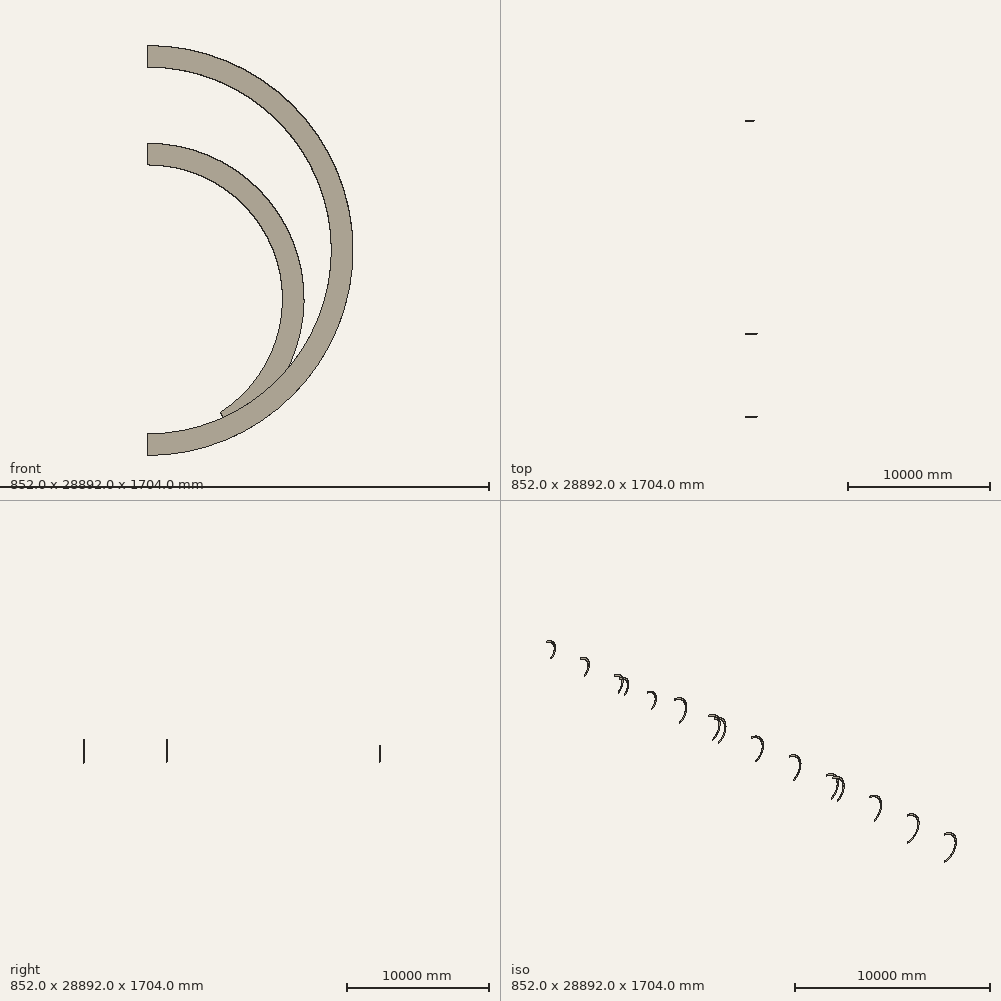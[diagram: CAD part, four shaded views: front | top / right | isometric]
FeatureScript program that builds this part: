
annotation { "Feature Type Name" : "Feature", "Feature Type Description" : "" }
export const myFeature = defineFeature(function(context is Context, id is Id, definition is map)
    precondition{}
    {
        {
            var Q0;
            Q0=qCreatedBy(makeId("Front.planeOp"),FACE);
            var sketch = newSketch(context, id + "F0", { "sketchPlane" : qUnion([Q0])});
            skCircle(sketch, "E0", {"center": v(0, 0) * mm, "radius": 852 * mm});
            skCircle(sketch, "E1", {"center": v(0, 0) * mm, "radius": 762 * mm});
            skSolve(sketch);
        }
        {
            var Q0;
            Q0 = qSketchRegion(id + "F0", true);
            extrude(context, id + "F1", {"entities" : qUnion([Q0]), "oppositeDirection" : true, "depth" : 19776 * mm});
        }
        {
            var Q0;
            Q0=makeQuery(id+"F1.opExtrude","CAP_FACE",FACE,{"disambiguationData":[OSD([sQuery(id+"F0.wireOp",EDGE,"E0"),sQuery(id+"F0.wireOp",EDGE,"E1")])],"isStart":false});
            cPlane(context, id + "F2", {"entities" : qUnion([Q0]), "cplaneType" : CPlaneType.OFFSET, "offset" : 1988 * mm, "width" : 150 * mm, "height" : 150 * mm});
        }
        {
            var Q0;
            Q0=qCreatedBy(id+"F2.planeOp",FACE);
            var sketch = newSketch(context, id + "F3", { "sketchPlane" : qUnion([Q0])});
            skCircle(sketch, "E2", {"center": v(0, -203.2) * mm, "radius": 648.8 * mm});
            skCircle(sketch, "E3", {"center": v(0, -203.2) * mm, "radius": 558.8 * mm});
            skSolve(sketch);
        }
        {
            var Q0;
            Q0 = qSketchRegion(id + "F3", true);
            extrude(context, id + "F4", {"entities" : qUnion([Q0]), "operationType" : NewBodyOperationType.ADD, "depth" : 7332 * mm});
        }
        {
            var Q0;
            Q0=qCreatedBy(makeId("Top.planeOp"),FACE);
            var sketch = newSketch(context, id + "F5", { "sketchPlane" : qUnion([Q0])});
            skLineSegment(sketch, "E4.bottom", {"start": v(0, 0) * mm, "end": v(-2899.89, 0) * mm});
            skLineSegment(sketch, "E4.top", {"start": v(0, 29096) * mm, "end": v(-2899.89, 29096) * mm});
            skLineSegment(sketch, "E4.left", {"start": v(0, 0) * mm, "end": v(0, 29096) * mm});
            skLineSegment(sketch, "E4.right", {"start": v(-2899.89, 0) * mm, "end": v(-2899.89, 29096) * mm});
            skSolve(sketch);
        }
        {
            var Q0;
            Q0 = qSketchRegion(id + "F5", true);
            extrude(context, id + "F6", {"entities" : qUnion([Q0]), "operationType" : NewBodyOperationType.REMOVE, "endBound" : BoundingType.THROUGH_ALL, "oppositeDirection" : true, "depth" : 25 * mm, "hasSecondDirection" : true, "secondDirectionBound" : SecondDirectionBoundingType.THROUGH_ALL, "secondDirectionOppositeDirection" : false, "secondDirectionDepth" : 25 * mm});
        }
        {
            var Q0;
            Q0=qCreatedBy(makeId("Right.planeOp"),FACE);
            var sketch = newSketch(context, id + "F7", { "sketchPlane" : qUnion([Q0])});
            skLineSegment(sketch, "E5.bottom", {"start": v(0, 852) * mm, "end": v(204, 852) * mm});
            skLineSegment(sketch, "E5.top", {"start": v(0, -852) * mm, "end": v(204, -852) * mm});
            skLineSegment(sketch, "E5.left", {"start": v(0, -852) * mm, "end": v(0, 852) * mm});
            skLineSegment(sketch, "E5.right", {"start": v(2914, -852) * mm, "end": v(2914, 852) * mm});
            skLineSegment(sketch, "E6.bottom", {"start": v(2926, -852) * mm, "end": v(5624, -852) * mm});
            skLineSegment(sketch, "E6.top", {"start": v(2926, 852) * mm, "end": v(5624, 852) * mm});
            skLineSegment(sketch, "E6.left", {"start": v(2926, 852) * mm, "end": v(2926, -852) * mm});
            skLineSegment(sketch, "E6.right", {"start": v(5624, 852) * mm, "end": v(5624, -852) * mm});
            skLineSegment(sketch, "E7.bottom", {"start": v(5636, -852) * mm, "end": v(8344, -852) * mm});
            skLineSegment(sketch, "E7.top", {"start": v(5636, 852) * mm, "end": v(8344, 852) * mm});
            skLineSegment(sketch, "E7.left", {"start": v(5636, 852) * mm, "end": v(5636, -852) * mm});
            skLineSegment(sketch, "E7.right", {"start": v(8344, 852) * mm, "end": v(8344, -852) * mm});
            skLineSegment(sketch, "E8.bottom", {"start": v(8356, -852) * mm, "end": v(8764, -852) * mm});
            skLineSegment(sketch, "E8.top", {"start": v(8356, 852) * mm, "end": v(8764, 852) * mm});
            skLineSegment(sketch, "E8.left", {"start": v(8356, 852) * mm, "end": v(8356, -852) * mm});
            skLineSegment(sketch, "E8.right", {"start": v(8764, 852) * mm, "end": v(8764, -852) * mm});
            skLineSegment(sketch, "E9.bottom", {"start": v(8776, -852) * mm, "end": v(11484, -852) * mm});
            skLineSegment(sketch, "E9.top", {"start": v(8776, 852) * mm, "end": v(11484, 852) * mm});
            skLineSegment(sketch, "E9.left", {"start": v(8776, 852) * mm, "end": v(8776, -852) * mm});
            skLineSegment(sketch, "E9.right", {"start": v(11484, 852) * mm, "end": v(11484, -852) * mm});
            skLineSegment(sketch, "E10.bottom", {"start": v(11496, -852) * mm, "end": v(14204, -852) * mm});
            skLineSegment(sketch, "E10.top", {"start": v(11496, 852) * mm, "end": v(14204, 852) * mm});
            skLineSegment(sketch, "E10.left", {"start": v(11496, 852) * mm, "end": v(11496, -852) * mm});
            skLineSegment(sketch, "E10.right", {"start": v(14204, 852) * mm, "end": v(14204, -852) * mm});
            skLineSegment(sketch, "E11.bottom", {"start": v(14216, -852) * mm, "end": v(16924, -852) * mm});
            skLineSegment(sketch, "E11.top", {"start": v(14216, 852) * mm, "end": v(16924, 852) * mm});
            skLineSegment(sketch, "E11.left", {"start": v(14216, 852) * mm, "end": v(14216, -852) * mm});
            skLineSegment(sketch, "E11.right", {"start": v(16924, 852) * mm, "end": v(16924, -852) * mm});
            skLineSegment(sketch, "E12.bottom", {"start": v(16936, -852) * mm, "end": v(17344, -852) * mm});
            skLineSegment(sketch, "E12.top", {"start": v(16936, 852) * mm, "end": v(17344, 852) * mm});
            skLineSegment(sketch, "E12.left", {"start": v(16936, 852) * mm, "end": v(16936, -852) * mm});
            skLineSegment(sketch, "E12.right", {"start": v(17344, 852) * mm, "end": v(17344, -852) * mm});
            skLineSegment(sketch, "E13.bottom", {"start": v(17356, -852) * mm, "end": v(19764, -852) * mm});
            skLineSegment(sketch, "E13.top", {"start": v(17356, 852) * mm, "end": v(19764, 852) * mm});
            skLineSegment(sketch, "E13.left", {"start": v(17356, 852) * mm, "end": v(17356, -852) * mm});
            skLineSegment(sketch, "E13.right", {"start": v(19764, 852) * mm, "end": v(19764, -852) * mm});
            skLineSegment(sketch, "E14.bottom", {"start": v(21776, -852) * mm, "end": v(23764, -852) * mm});
            skLineSegment(sketch, "E14.top", {"start": v(21776, 852) * mm, "end": v(23764, 852) * mm});
            skLineSegment(sketch, "E14.left", {"start": v(21776, 852) * mm, "end": v(21776, -852) * mm});
            skLineSegment(sketch, "E14.right", {"start": v(23764, 852) * mm, "end": v(23764, -852) * mm});
            skLineSegment(sketch, "E15.bottom", {"start": v(23776, -852) * mm, "end": v(24184, -852) * mm});
            skLineSegment(sketch, "E15.top", {"start": v(23776, 852) * mm, "end": v(24184, 852) * mm});
            skLineSegment(sketch, "E15.left", {"start": v(23776, 852) * mm, "end": v(23776, -852) * mm});
            skLineSegment(sketch, "E15.right", {"start": v(24184, 852) * mm, "end": v(24184, -852) * mm});
            skLineSegment(sketch, "E16.bottom", {"start": v(24196, -852) * mm, "end": v(26634, -852) * mm});
            skLineSegment(sketch, "E16.top", {"start": v(24196, 852) * mm, "end": v(26634, 852) * mm});
            skLineSegment(sketch, "E16.left", {"start": v(24196, 852) * mm, "end": v(24196, -852) * mm});
            skLineSegment(sketch, "E16.right", {"start": v(26634, 852) * mm, "end": v(26634, -852) * mm});
            skLineSegment(sketch, "E17.bottom", {"start": v(26646, -852) * mm, "end": v(29084, -852) * mm});
            skLineSegment(sketch, "E17.top", {"start": v(26646, 852) * mm, "end": v(29084, 852) * mm});
            skLineSegment(sketch, "E17.left", {"start": v(26646, 852) * mm, "end": v(26646, -852) * mm});
            skLineSegment(sketch, "E17.right", {"start": v(29084, 852) * mm, "end": v(29084, -852) * mm});
            skLineSegment(sketch, "E18.left", {"start": v(204, 852) * mm, "end": v(204, -852) * mm});
            skLineSegment(sketch, "E18.right", {"start": v(216, 852) * mm, "end": v(216, -852) * mm});
            skLineSegment(sketch, "E19.trimOffspring", {"start": v(216, 852) * mm, "end": v(2914, 852) * mm});
            skLineSegment(sketch, "E20.trimOffspring", {"start": v(216, -852) * mm, "end": v(2914, -852) * mm});
            skSolve(sketch);
        }
        {
            var Q0;
            Q0 = qSketchRegion(id + "F7", true);
            extrude(context, id + "F8", {"entities" : qUnion([Q0]), "operationType" : NewBodyOperationType.REMOVE, "endBound" : BoundingType.THROUGH_ALL, "depth" : 25 * mm});
        }
        {
            var Q0;
            Q0=makeQuery(id+"F8.boolean.opBoolean","COPY",FACE,{"derivedFrom":makeQuery(id+"F8.opExtrude","SWEPT_FACE",FACE,{"disambiguationData":[OSD([sQuery(id+"F7.wireOp",EDGE,"E6.right")])]})});
            var sketch = newSketch(context, id + "F9", { "sketchPlane" : qUnion([Q0])});
            skLineSegment(sketch, "E21", {"start": v(0, -980) * mm, "end": v(110.64, -980) * mm});
            skLineSegment(sketch, "E22", {"start": v(110.64, -980) * mm, "end": v(120.64, -997.32) * mm});
            skLineSegment(sketch, "E23", {"start": v(120.64, -997.32) * mm, "end": v(396.07, -838.3) * mm});
            skLineSegment(sketch, "E24", {"start": v(396.07, -838.3) * mm, "end": v(0, -152.29) * mm});
            skLineSegment(sketch, "E25", {"start": v(0, -152.29) * mm, "end": v(0, -980) * mm});
            skSolve(sketch);
        }
        {
            var Q0;
            Q0 = qSketchRegion(id + "F9", true);
            extrude(context, id + "F10", {"entities" : qUnion([Q0]), "operationType" : NewBodyOperationType.REMOVE, "endBound" : BoundingType.THROUGH_ALL, "oppositeDirection" : true, "depth" : 25 * mm});
        }
    });
